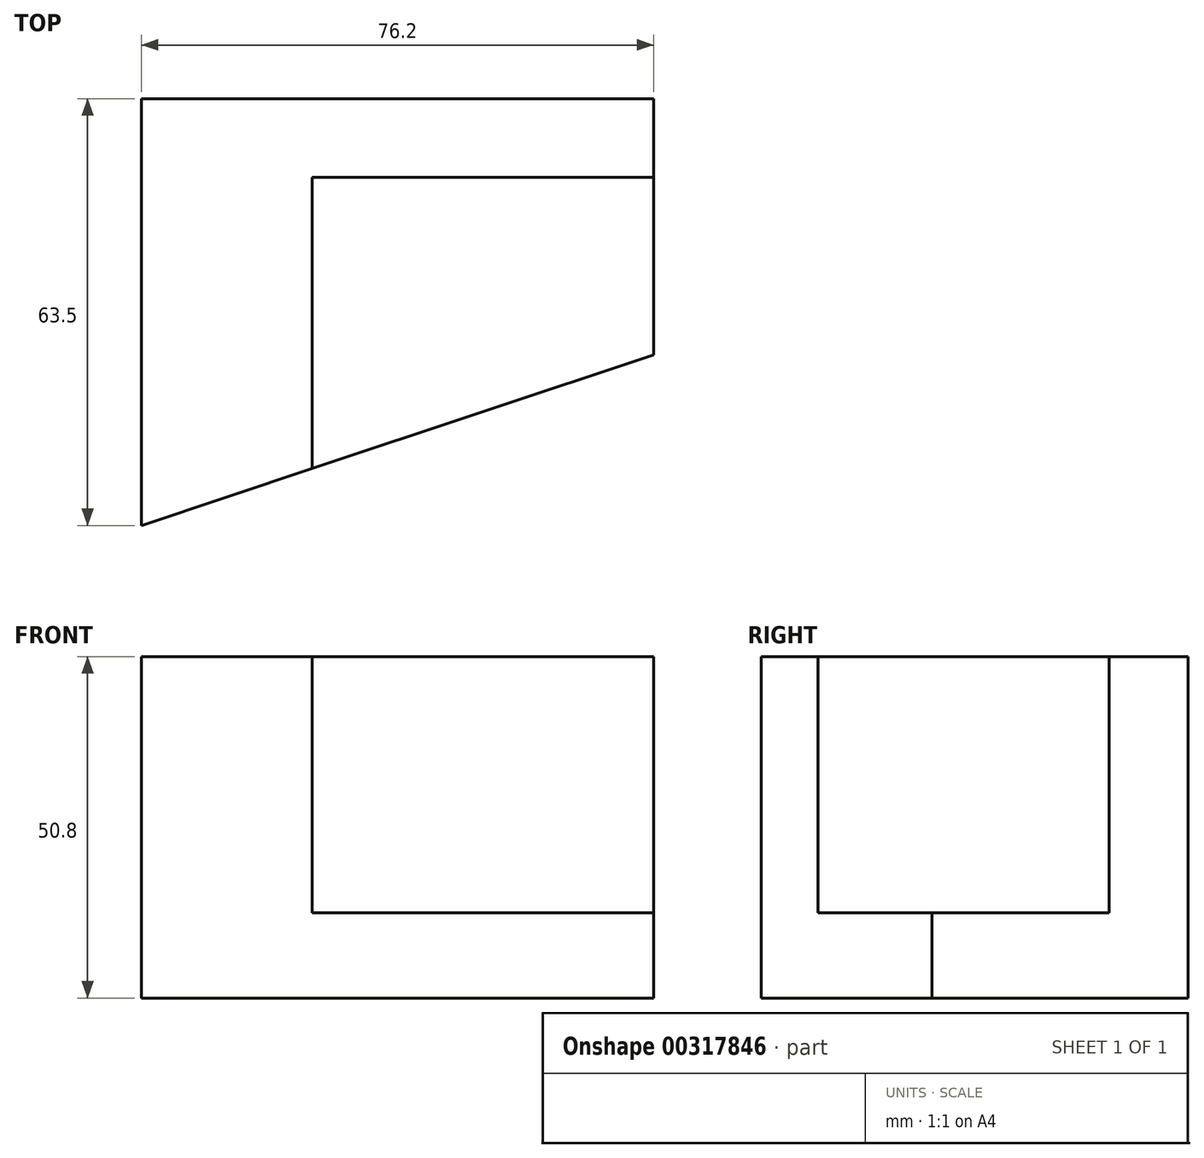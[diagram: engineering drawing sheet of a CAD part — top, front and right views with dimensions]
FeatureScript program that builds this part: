
annotation { "Feature Type Name" : "Feature", "Feature Type Description" : "" }
export const myFeature = defineFeature(function(context is Context, id is Id, definition is map)
    precondition{}
    {
        {
            var Q0;
            Q0=qCreatedBy(makeId("Top.planeOp"),FACE);
            var sketch = newSketch(context, id + "F0", { "sketchPlane" : qUnion([Q0])});
            skLineSegment(sketch, "E0", {"start": v(0, 63.5) * mm, "end": v(0, 0) * mm});
            skLineSegment(sketch, "E1", {"start": v(0, 63.5) * mm, "end": v(76.2, 63.5) * mm});
            skLineSegment(sketch, "E2", {"start": v(76.2, 63.5) * mm, "end": v(76.2, 25.4) * mm});
            skLineSegment(sketch, "E3", {"start": v(76.2, 25.4) * mm, "end": v(0, 0) * mm});
            skSolve(sketch);
        }
        {
            var Q0;
            Q0=makeQuery(id+"F0.imprint","IMPRINT",FACE,{"disambiguationData":[TD([[makeQuery(id+"F0.imprint","IMPRINT",EDGE,{"derivedFrom":sQuery(id+"F0.wireOp",EDGE,"E0")}),1.0]])]});
            extrude(context, id + "F1", {"entities" : qUnion([Q0]), "depth" : 50.8 * mm});
        }
        {
            var Q0;
            Q0=makeQuery(id+"F1.opExtrude","CAP_FACE",FACE,{"disambiguationData":[OSD([sQuery(id+"F0.wireOp",EDGE,"E0"),sQuery(id+"F0.wireOp",EDGE,"E1"),sQuery(id+"F0.wireOp",EDGE,"E2"),sQuery(id+"F0.wireOp",EDGE,"E3")])],"isStart":false});
            var sketch = newSketch(context, id + "F2", { "sketchPlane" : qUnion([Q0])});
            skLineSegment(sketch, "E4", {"start": v(76.2, 51.76) * mm, "end": v(25.4, 51.76) * mm});
            skLineSegment(sketch, "E5", {"start": v(25.4, 51.76) * mm, "end": v(25.4, 8.47) * mm});
            skSolve(sketch);
        }
        {
            var Q0;
            {var subQ0=sQuery(id+"F2.wireOp",EDGE,"E4");Q0=makeQuery(id+"F2.imprint","IMPRINT",FACE,{"disambiguationData":[TD([[makeQuery(id+"F2.imprint","IMPRINT",EDGE,{"derivedFrom":subQ0}),1.0]])]});}
            extrude(context, id + "F3", {"entities" : qUnion([Q0]), "operationType" : NewBodyOperationType.REMOVE, "oppositeDirection" : true, "depth" : 38.1 * mm});
        }
    });
